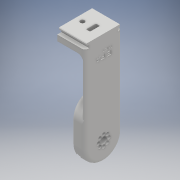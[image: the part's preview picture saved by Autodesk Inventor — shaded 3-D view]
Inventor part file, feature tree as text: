
AUTODESK INVENTOR PART (.ipt)
format: ipt  version: 2018 (Build 220112000, 112)  size: 1,395,200 bytes
history: native  units: mm
features: sketch x10, fillet x7, projected_geometry x5, extrude x4, hole x2, emboss x2, mirror x1, sweep x1
ambient origin geometry x8: Origin, YZ Plane, XZ Plane, XY Plane, X Axis, Y Axis, Z Axis, Center Point
bodies: Solid1 (feature_tree)
feature tree (32):
  extrude  "Extrusion1"  Depth=200.0mm
  extrude  "Extrusion2"  Depth=10.0mm
  fillet  "Fillet1"  Radius=37.0mm
  extrude  "Extrusion3"  Depth=32.0mm
  hole  "Hole1"  [1 undecoded]
  hole  "Hole2"  [1 undecoded]
  fillet  "Fillet2"  Radius=15.5mm
  extrude  "Extrusion4"  Depth=0.5mm TaperAngle=0.0deg
  mirror  "Mirror1"
  fillet  "Fillet3"  Radius=4.0mm
  emboss  "Emboss1"
  fillet  "Fillet5"  Radius=28.0mm
  sweep  "Sweep5"
  fillet  "Fillet10"  Radius=13.0mm
  fillet  "Fillet11"  Radius=9.0mm
  fillet  "Fillet12"  Radius=65.0mm
  emboss  "Emboss2"
  sketch  "Sketch1"  dims[d0=0.3mm d2=200.0mm]
  sketch  "Sketch2"  dims[d3=5.0mm d4=0.0mm d5=10.0mm d6=37.0mm d7=0.0mm]
  projected_geometry  "Projected Loop1"
  sketch  "Sketch3"  dims[d8=6.0mm d9=32.0mm]
  projected_geometry  "Projected Loop2"
  sketch  "Sketch4"  dims[d10=15.5mm d11=0.0mm]
  projected_geometry  "Projected Loop3"
  sketch  "Sketch5"  dims[d12=5.0mm d13=6.0mm d14=4.0mm d15=2.0mm d16=90.0deg d17=16.5mm d18=20.594885mm d19=180.0deg]
  projected_geometry  "Projected Loop4"
  sketch  "Sketch6"  dims[d21=6.6mm d22=6.0mm d23=12.0mm d24=8.0mm d25=14.3117mm d26=16.5mm d27=20.594885mm d28=5.0mm d29=15.5mm d30=0.0mm]
  sketch  "Sketch8"  dims[d31=2.0mm d39=0.5mm d40=0.0mm d41=4.0mm d42=28.0mm]
  sketch  "Sketch9"  dims[d43=15.0mm d44=6.0mm d45=13.0mm d89=9.0mm d90=65.0mm]
  projected_geometry  "Projected Loop6"
  sketch  "3D Sketch3"
  sketch  "Sketch13"  dims[d99=14.0mm d101=10.0mm d102=16.0mm d103=10.0mm d104=29.670597mm d105=16.0mm d106=20.0mm d107=10.0mm d108=8.0mm d109=120.0deg d110=0.0mm d111=0.0mm d112=1.0mm d113=0.2mm d114=1.0mm d115=1.0mm d116=0.0mm]
note: 2 required parameter values undecoded (feature->parameter linkage not recoverable at this tier; creation-order binding heuristic only, values carry confidence <= 0.55)
